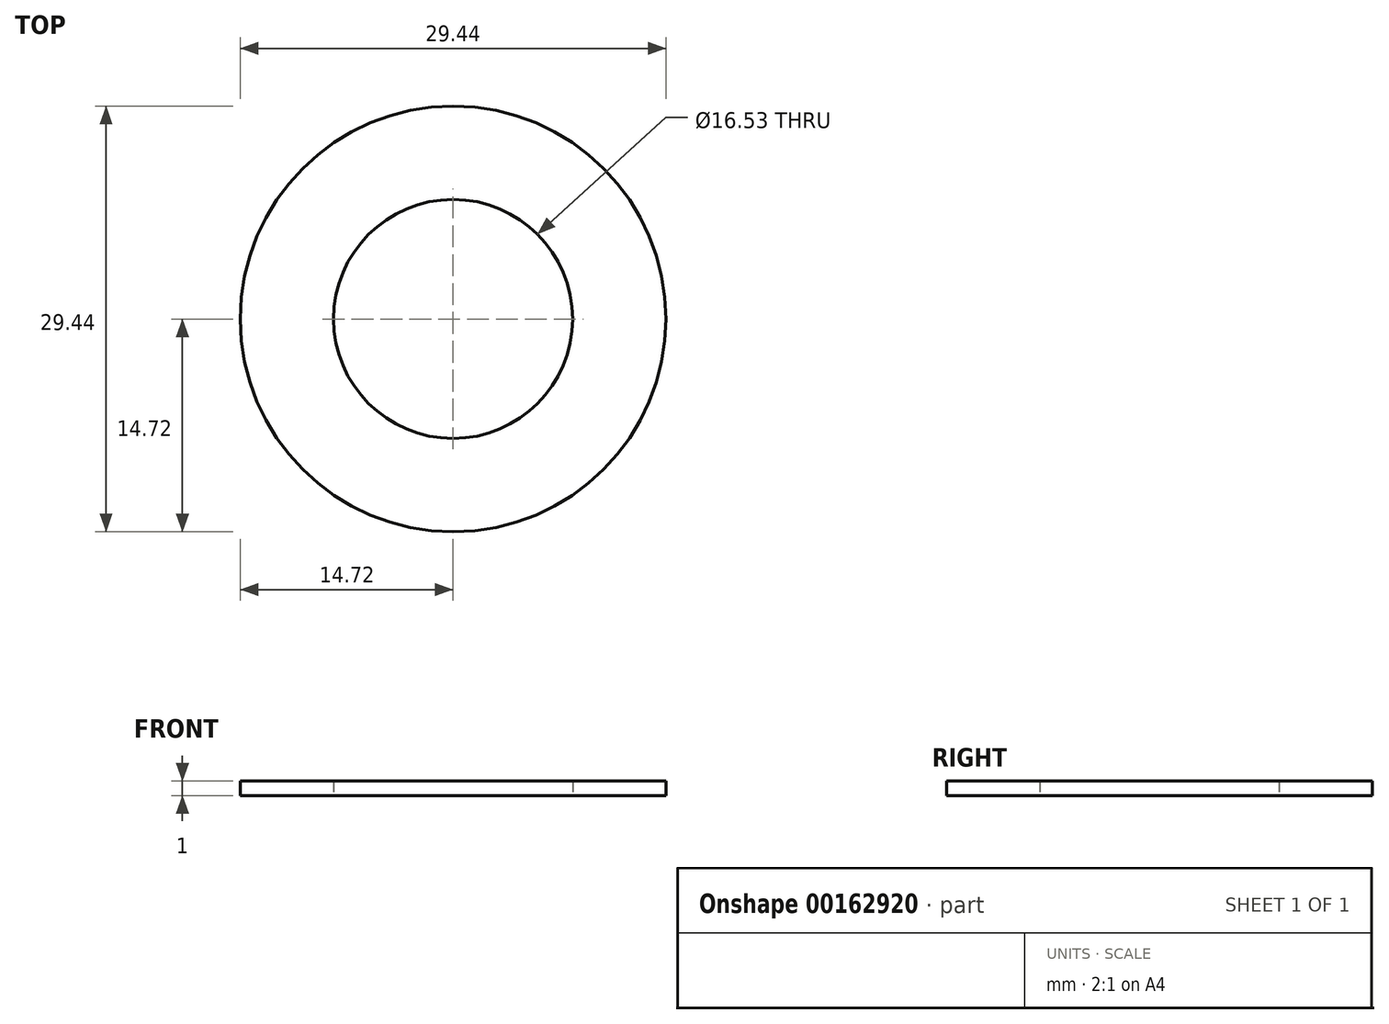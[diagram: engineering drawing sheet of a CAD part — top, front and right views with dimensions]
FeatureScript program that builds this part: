
annotation { "Feature Type Name" : "Feature", "Feature Type Description" : "" }
export const myFeature = defineFeature(function(context is Context, id is Id, definition is map)
    precondition{}
    {
        {
            var Q0;
            Q0=qCreatedBy(makeId("Top.planeOp"),FACE);
            var sketch = newSketch(context, id + "F0", { "sketchPlane" : qUnion([Q0])});
            skCircle(sketch, "E0", {"center": v(0, 0) * mm, "radius": 8.27 * mm});
            skCircle(sketch, "E1", {"center": v(0, 0) * mm, "radius": 14.72 * mm});
            skSolve(sketch);
        }
        {
            var Q0;
            Q0=qSketchRegion(id+"F0",true);
            extrude(context, id + "F1", {"entities" : qUnion([Q0]), "depth" : 1 * mm});
        }
    });
